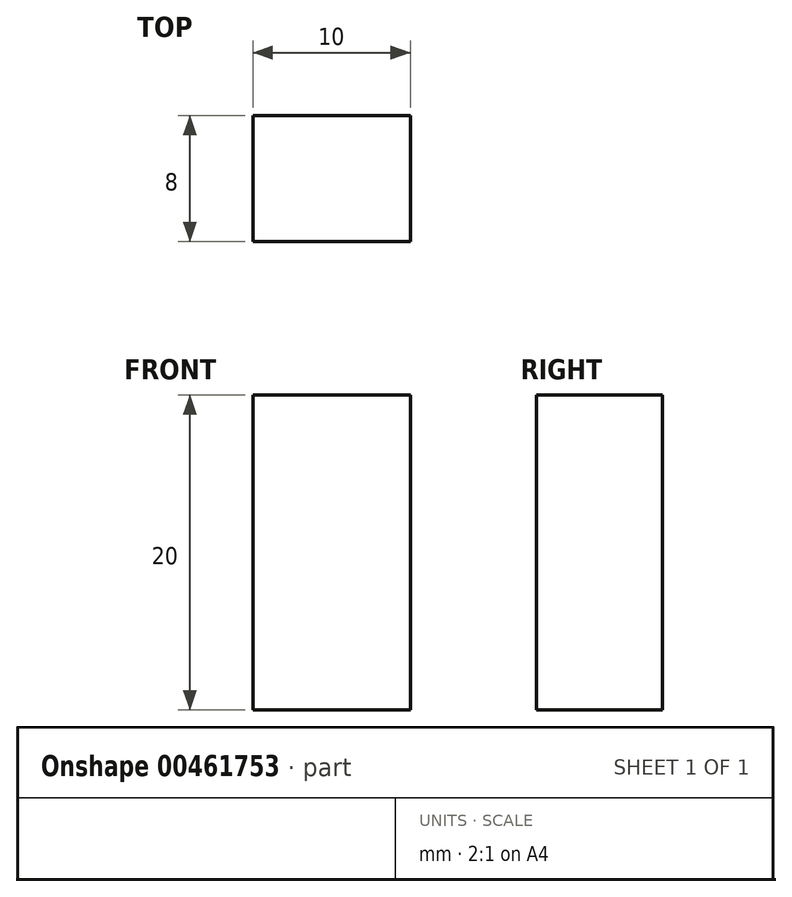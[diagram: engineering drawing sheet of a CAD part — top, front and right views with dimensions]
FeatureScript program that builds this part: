
annotation { "Feature Type Name" : "Feature", "Feature Type Description" : "" }
export const myFeature = defineFeature(function(context is Context, id is Id, definition is map)
    precondition{}
    {
        {
            var Q0;
            Q0=qCreatedBy(makeId("Top.planeOp"),FACE);
            var sketch = newSketch(context, id + "F0", { "sketchPlane" : qUnion([Q0])});
            skLineSegment(sketch, "E0.bottom", {"start": v(5, -4) * mm, "end": v(-5, -4) * mm});
            skLineSegment(sketch, "E0.top", {"start": v(5, 4) * mm, "end": v(-5, 4) * mm});
            skLineSegment(sketch, "E0.left", {"start": v(5, -4) * mm, "end": v(5, 4) * mm});
            skLineSegment(sketch, "E0.right", {"start": v(-5, -4) * mm, "end": v(-5, 4) * mm});
            skPoint(sketch, "E0.middle", {"position": v(0, 0) * mm});
            skSolve(sketch);
        }
        {
            var Q0;
            Q0=makeQuery(id+"F0.imprint","IMPRINT",FACE,{"disambiguationData":[TD([[makeQuery(id+"F0.imprint","IMPRINT",EDGE,{"derivedFrom":sQuery(id+"F0.wireOp",EDGE,"E0.bottom")}),-1.0]])]});
            extrude(context, id + "F1", {"entities" : qUnion([Q0]), "depth" : 20 * mm});
        }
    });
